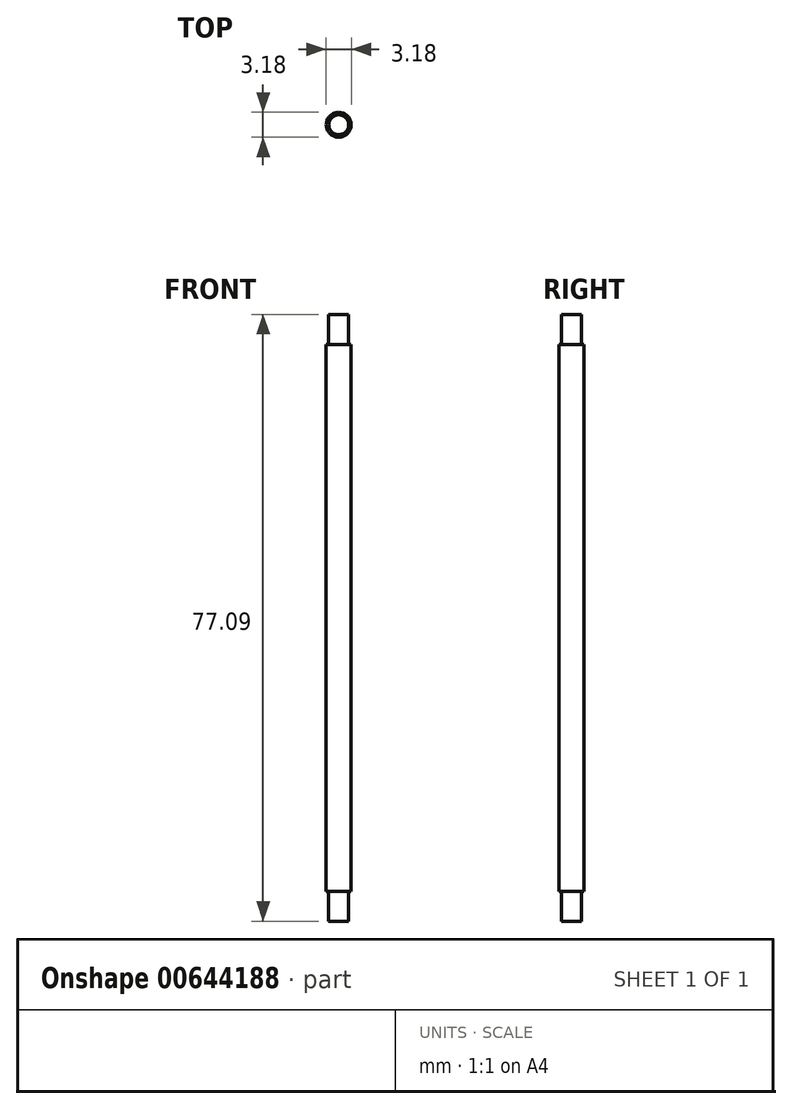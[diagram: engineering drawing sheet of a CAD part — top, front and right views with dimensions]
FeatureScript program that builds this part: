
annotation { "Feature Type Name" : "Feature", "Feature Type Description" : "" }
export const myFeature = defineFeature(function(context is Context, id is Id, definition is map)
    precondition{}
    {
        {
            var Q0;
            Q0=qCreatedBy(makeId("Front.planeOp"),FACE);
            var sketch = newSketch(context, id + "F0", { "sketchPlane" : qUnion([Q0])});
            skLineSegment(sketch, "E0.bottom", {"start": v(0, 0) * mm, "end": v(-1.59, 0) * mm});
            skLineSegment(sketch, "E0.top", {"start": v(0, 69.47) * mm, "end": v(-1.59, 69.47) * mm});
            skLineSegment(sketch, "E0.left", {"start": v(0, 0) * mm, "end": v(0, 69.47) * mm});
            skLineSegment(sketch, "E0.right", {"start": v(-1.59, 0) * mm, "end": v(-1.59, 69.47) * mm});
            skLineSegment(sketch, "E1.bottom", {"start": v(0, 0) * mm, "end": v(-1.27, 0) * mm});
            skLineSegment(sketch, "E1.top", {"start": v(0, -3.81) * mm, "end": v(-1.27, -3.81) * mm});
            skLineSegment(sketch, "E1.left", {"start": v(0, 0) * mm, "end": v(0, -3.81) * mm});
            skLineSegment(sketch, "E1.right", {"start": v(-1.27, 0) * mm, "end": v(-1.27, -3.81) * mm});
            skLineSegment(sketch, "E2.bottom", {"start": v(0, 69.47) * mm, "end": v(-1.27, 69.47) * mm});
            skLineSegment(sketch, "E2.top", {"start": v(0, 73.28) * mm, "end": v(-1.27, 73.28) * mm});
            skLineSegment(sketch, "E2.left", {"start": v(0, 69.47) * mm, "end": v(0, 73.28) * mm});
            skLineSegment(sketch, "E2.right", {"start": v(-1.27, 69.47) * mm, "end": v(-1.27, 73.28) * mm});
            skSolve(sketch);
        }
        {
            var Q0;
            Q0 = qSketchRegion(id + "F0", true);
            var Q1;
            Q1=sQuery(id+"F0.wireOp",EDGE,"E0.left");
            revolve(context, id + "F1", {"entities" : qUnion([Q0]), "axis" : qUnion([Q1]), "revolveType" : RevolveType.FULL});
        }
    });
